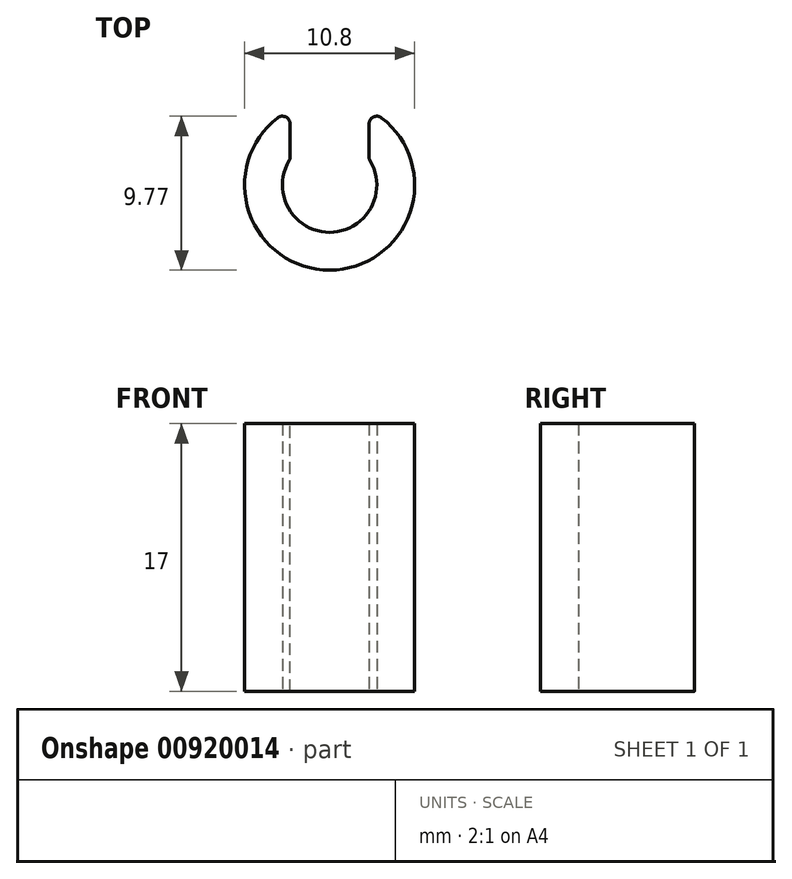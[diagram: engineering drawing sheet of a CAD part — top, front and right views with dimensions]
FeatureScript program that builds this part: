
annotation { "Feature Type Name" : "Feature", "Feature Type Description" : "" }
export const myFeature = defineFeature(function(context is Context, id is Id, definition is map)
    precondition{}
    {
        {
            var Q0;
            Q0=qCreatedBy(makeId("Top.planeOp"),FACE);
            var sketch = newSketch(context, id + "F0", { "sketchPlane" : qUnion([Q0])});
            skCircle(sketch, "E0", {"center": v(0, 0) * mm, "radius": 5.4 * mm});
            skCircle(sketch, "E1", {"center": v(0, 0) * mm, "radius": 3 * mm});
            skLineSegment(sketch, "E2", {"start": v(-2.5, 4.79) * mm, "end": v(-2.5, 1.66) * mm});
            skLineSegment(sketch, "E3", {"start": v(2.5, 1.66) * mm, "end": v(2.5, 4.79) * mm});
            skSolve(sketch);
        }
        {
            var Q0;
            {var subQ0=sQuery(id+"F0.wireOp",EDGE,"E2");Q0=makeQuery(id+"F0.imprint","IMPRINT",FACE,{"disambiguationData":[TD([[makeQuery(id+"F0.imprint","IMPRINT",EDGE,{"derivedFrom":subQ0}),-1.0]])]});}
            extrude(context, id + "F1", {"entities" : qUnion([Q0]), "depth" : 17 * mm, "offsetDistance" : 25 * mm});
        }
        {
            var Q0;
            Q0=makeQuery(id+"F1.opExtrude","SWEPT_EDGE",EDGE,{"disambiguationData":[OSD([sQuery(id+"F0.wireOp",EDGE,"E0"),sQuery(id+"F0.wireOp",EDGE,"E3")])]});
            var Q1;
            Q1=makeQuery(id+"F1.opExtrude","SWEPT_EDGE",EDGE,{"disambiguationData":[OSD([sQuery(id+"F0.wireOp",EDGE,"E1"),sQuery(id+"F0.wireOp",EDGE,"E3")])]});
            var Q2;
            Q2=makeQuery(id+"F1.opExtrude","SWEPT_EDGE",EDGE,{"disambiguationData":[OSD([sQuery(id+"F0.wireOp",EDGE,"E1"),sQuery(id+"F0.wireOp",EDGE,"E2")])]});
            var Q3;
            Q3=makeQuery(id+"F1.opExtrude","SWEPT_EDGE",EDGE,{"disambiguationData":[OSD([sQuery(id+"F0.wireOp",EDGE,"E0"),sQuery(id+"F0.wireOp",EDGE,"E2")])]});
            fillet(context, id + "F2", {"entities" : qUnion([Q0, Q1, Q2, Q3]), "radius" : 0.5 * mm, "tangentPropagation" : true, "allowEdgeOverflow" : false});
        }
    });
